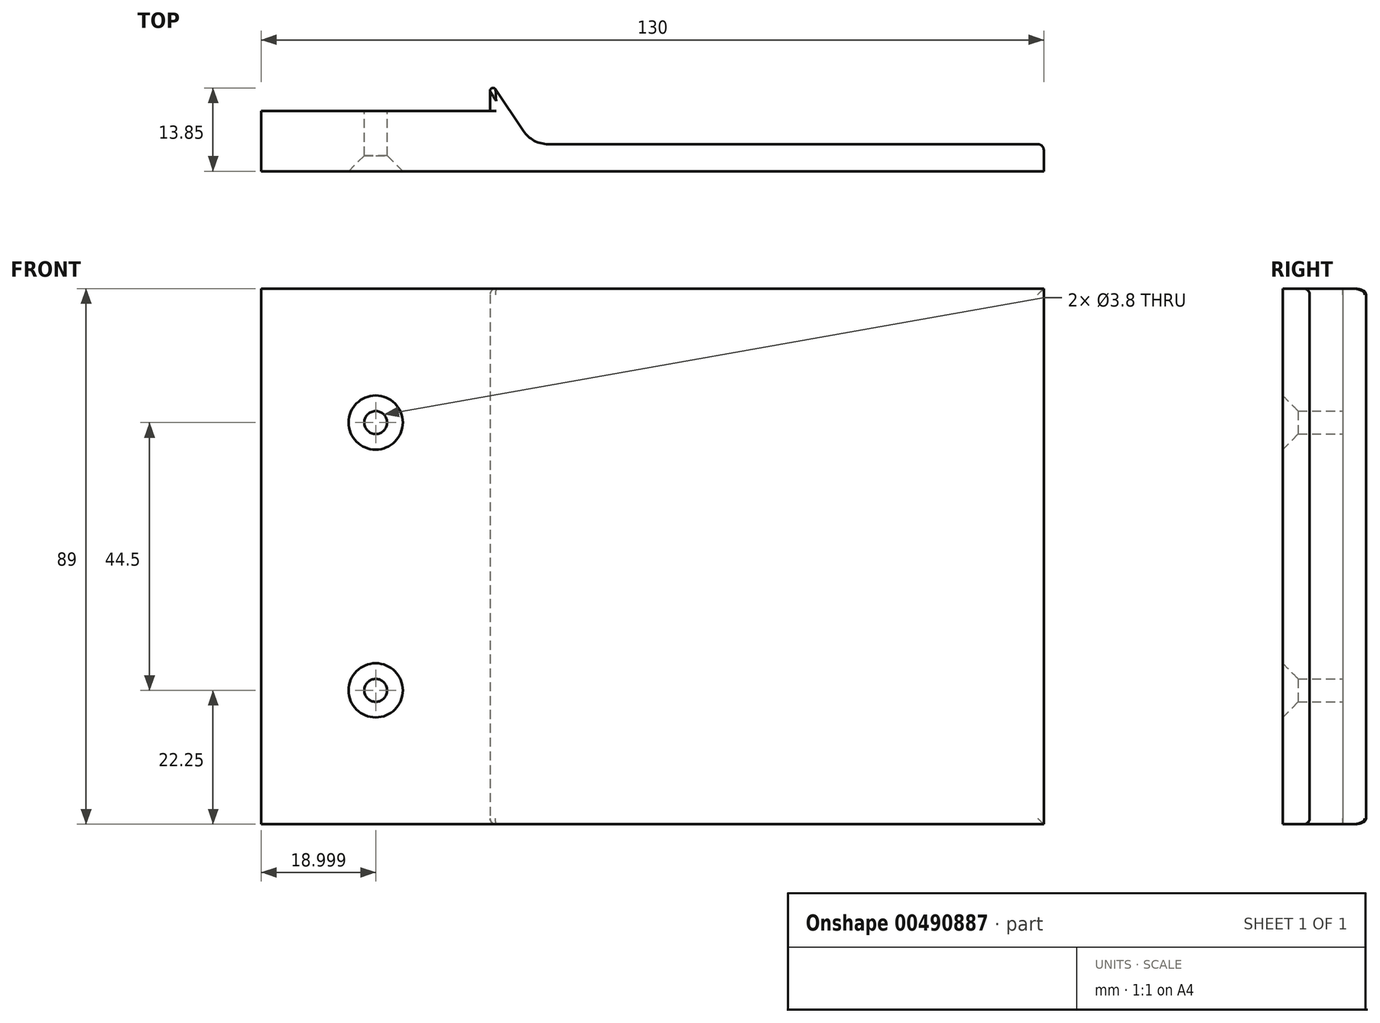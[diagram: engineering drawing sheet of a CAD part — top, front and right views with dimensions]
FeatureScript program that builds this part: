
annotation { "Feature Type Name" : "Feature", "Feature Type Description" : "" }
export const myFeature = defineFeature(function(context is Context, id is Id, definition is map)
    precondition{}
    {
        {
            var Q0;
            Q0=qCreatedBy(makeId("Top.planeOp"),FACE);
            var sketch = newSketch(context, id + "F0", { "sketchPlane" : qUnion([Q0])});
            skLineSegment(sketch, "E0", {"start": v(-54.55, 0) * mm, "end": v(75.45, 0) * mm});
            skLineSegment(sketch, "E1", {"start": v(75.45, 0) * mm, "end": v(75.45, 4.5) * mm});
            skLineSegment(sketch, "E2", {"start": v(-54.55, 0) * mm, "end": v(-54.55, 10) * mm});
            skLineSegment(sketch, "E3", {"start": v(-54.55, 10) * mm, "end": v(-16.55, 10) * mm});
            skLineSegment(sketch, "E4", {"start": v(-16.55, 10) * mm, "end": v(-16.55, 15) * mm});
            skLineSegment(sketch, "E5", {"start": v(-16.55, 0) * mm, "end": v(-16.55, 10) * mm, "construction": true});
            skLineSegment(sketch, "E6", {"start": v(75.45, 4.5) * mm, "end": v(-9.55, 4.5) * mm});
            skLineSegment(sketch, "E7", {"start": v(-9.55, 4.5) * mm, "end": v(-16.55, 15) * mm});
            skSolve(sketch);
        }
        {
            var Q0;
            Q0=makeQuery(id+"F0.imprint","IMPRINT",FACE,{"disambiguationData":[TD([[makeQuery(id+"F0.imprint","IMPRINT",EDGE,{"derivedFrom":sQuery(id+"F0.wireOp",EDGE,"E0")}),1.0]])]});
            extrude(context, id + "F1", {"entities" : qUnion([Q0]), "endBound" : BoundingType.SYMMETRIC, "depth" : 89 * mm});
        }
        {
            var Q0;
            Q0=makeQuery(id+"F1.opExtrude","SWEPT_FACE",FACE,{"disambiguationData":[OSD([sQuery(id+"F0.wireOp",EDGE,"E3")])]});
            var sketch = newSketch(context, id + "F2", { "sketchPlane" : qUnion([Q0])});
            skLineSegment(sketch, "E8", {"start": v(35.55, -44.5) * mm, "end": v(35.55, 44.5) * mm, "construction": true});
            skLineSegment(sketch, "E9", {"start": v(54.55, -44.5) * mm, "end": v(16.55, 0) * mm, "construction": true});
            skLineSegment(sketch, "E10", {"start": v(16.55, -44.5) * mm, "end": v(54.55, 0) * mm, "construction": true});
            skLineSegment(sketch, "E11", {"start": v(54.55, 0) * mm, "end": v(16.55, 44.5) * mm, "construction": true});
            skLineSegment(sketch, "E12", {"start": v(54.55, 44.5) * mm, "end": v(16.55, 0) * mm, "construction": true});
            skCircle(sketch, "E13", {"center": v(35.55, -22.25) * mm, "radius": 1.9 * mm});
            skCircle(sketch, "E14", {"center": v(35.55, 22.25) * mm, "radius": 1.9 * mm});
            skSolve(sketch);
        }
        {
            var Q0;
            Q0 = qSketchRegion(id + "F2", true);
            extrude(context, id + "F3", {"entities" : qUnion([Q0]), "operationType" : NewBodyOperationType.REMOVE, "oppositeDirection" : true, "depth" : 25 * mm});
        }
        {
            var Q0;
            Q0=makeQuery(id+"F3.boolean.opBoolean","INTERSECT",EDGE,{"derivedFrom":[makeQuery(id+"F1.opExtrude","SWEPT_FACE",FACE,{"disambiguationData":[OSD([sQuery(id+"F0.wireOp",EDGE,"E0")])]}),makeQuery(id+"F3.opExtrude","SWEPT_FACE",FACE,{"disambiguationData":[OSD([sQuery(id+"F2.wireOp",EDGE,"E14")])]})]});
            var Q1;
            Q1=makeQuery(id+"F3.boolean.opBoolean","INTERSECT",EDGE,{"derivedFrom":[makeQuery(id+"F1.opExtrude","SWEPT_FACE",FACE,{"disambiguationData":[OSD([sQuery(id+"F0.wireOp",EDGE,"E0")])]}),makeQuery(id+"F3.opExtrude","SWEPT_FACE",FACE,{"disambiguationData":[OSD([sQuery(id+"F2.wireOp",EDGE,"E13")])]})]});
            chamfer(context, id + "F4", {"entities" : qUnion([Q0, Q1]), "width" : 2.6 * mm, "tangentPropagation" : true});
        }
        {
            var Q0;
            Q0=makeQuery(id+"F1.opExtrude","SWEPT_EDGE",EDGE,{"disambiguationData":[OSD([sQuery(id+"F0.wireOp",EDGE,"E4"),sQuery(id+"F0.wireOp",EDGE,"E7")])]});
            fillet(context, id + "F5", {"entities" : qUnion([Q0]), "radius" : .5 * mm, "tangentPropagation" : true, "allowEdgeOverflow" : false});
        }
        {
            var Q0;
            Q0=makeQuery(id+"F1.opExtrude","SWEPT_EDGE",EDGE,{"disambiguationData":[OSD([sQuery(id+"F0.wireOp",EDGE,"E6"),sQuery(id+"F0.wireOp",EDGE,"E7")])]});
            fillet(context, id + "F6", {"entities" : qUnion([Q0]), "radius" : 5 * mm, "tangentPropagation" : true, "allowEdgeOverflow" : false});
        }
        {
            var Q0;
            Q0=makeQuery(id+"F1.opExtrude","CAP_EDGE",EDGE,{"disambiguationData":[OSD([sQuery(id+"F0.wireOp",EDGE,"E6")])],"isStart":false});
            var Q1;
            Q1=makeQuery(id+"F1.opExtrude","SWEPT_EDGE",EDGE,{"disambiguationData":[OSD([sQuery(id+"F0.wireOp",EDGE,"E1"),sQuery(id+"F0.wireOp",EDGE,"E6")])]});
            var Q2;
            Q2=makeQuery(id+"F1.opExtrude","CAP_EDGE",EDGE,{"disambiguationData":[OSD([sQuery(id+"F0.wireOp",EDGE,"E6")])],"isStart":true});
            fillet(context, id + "F7", {"entities" : qUnion([Q0, Q1, Q2]), "radius" : 1 * mm, "tangentPropagation" : true, "allowEdgeOverflow" : false});
        }
    });
